# Revit family: Sink-American_Standard-Quince-77SB33223.308
name_source: partatom
category: Plumbing Fixtures
revit_build: Autodesk Revit 2014 (Build: 20130308_1515(x64)
units: mm (PartAtom-declared; Revit-internal decimal feet)

## types (1)
- 77SB33223.308
    ADA Compliant = Yes
    Assembly Code = D2010410
    Basin Shape = Rectangular
    Bowl Length = 19 5/16"
    Bowl Width = 30 1/4"
    CW Connection = Yes
    CWFU = 3
    Cold Water Connection Diameter = 1/2"
    Cold Water Connection Radius = 1/4"
    Cold Water Connection Width = 4"
    Default Elevation = 34"
    Description = Quince Single Bowl Kitchen Sink
    Finish = Cast Iron-American Standard-308-Brilliant White
    HW Connection = Yes
    HWFU = 3
    Height = 9 3/8"
    Hole Height = 1"
    Hot Water Connection Diameter = 1"
    Hot Water Connection Radius = 1/4"
    Hot Water Connection Width = 4"
    Installation Type = Topmount
    Length = 22 1/16"
    Manufacturer = American Standard
    Material = Cast Iron-American Standard-308-Brilliant White
    Model = 77SB33223.308
    Price = Prices may vary. Please consult Manufacturer Representative for most up-to-date price list.
    Type Comments = 36" (914mm) cabinet required
    URL = https://www.americanstandard-us.com
    Vent Connection = No
    WFU = 4
    Warranty Information = Limited Lifetime Warranty
    Waste Connection = Yes
    Waste Connection Diameter = 1 1/2"
    Waste Connection Offset = 12"
    Waste Connection Radius = 3/4"
    Waste Connection Width = 15 1/8"
    Width = 33"

## geometry (parser evidence)
native form markers: Sweep x5
no freeform markers — native parametric forms only
